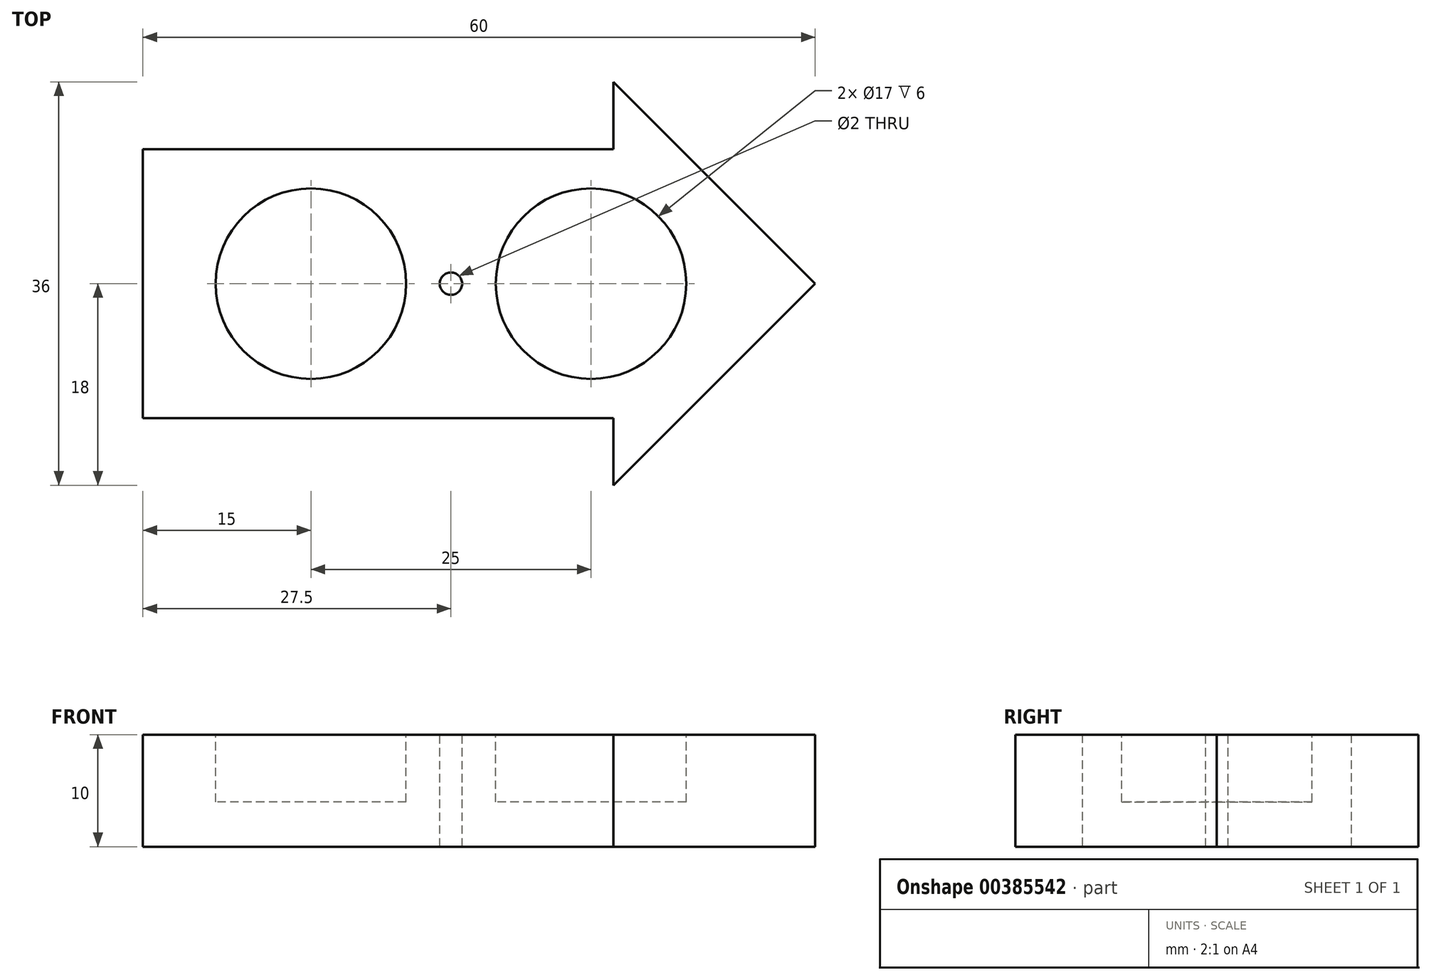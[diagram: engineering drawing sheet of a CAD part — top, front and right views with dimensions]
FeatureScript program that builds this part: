
annotation { "Feature Type Name" : "Feature", "Feature Type Description" : "" }
export const myFeature = defineFeature(function(context is Context, id is Id, definition is map)
    precondition{}
    {
        {
            var Q0;
            Q0=qCreatedBy(makeId("Top.planeOp"),FACE);
            var sketch = newSketch(context, id + "F0", { "sketchPlane" : qUnion([Q0])});
            skLineSegment(sketch, "E0.bottom", {"start": v(0, 0) * mm, "end": v(42, 0) * mm});
            skLineSegment(sketch, "E0.top", {"start": v(0, 24) * mm, "end": v(42, 24) * mm});
            skLineSegment(sketch, "E0.left", {"start": v(0, 0) * mm, "end": v(0, 24) * mm});
            skLineSegment(sketch, "E0.right", {"start": v(42, 0) * mm, "end": v(42, 24) * mm});
            skLineSegment(sketch, "E1.bottom", {"start": v(42, 30) * mm, "end": v(60, 30) * mm, "construction": true});
            skLineSegment(sketch, "E1.top", {"start": v(42, -6) * mm, "end": v(60, -6) * mm, "construction": true});
            skLineSegment(sketch, "E1.left", {"start": v(42, 30) * mm, "end": v(42, -6) * mm});
            skLineSegment(sketch, "E1.right", {"start": v(60, 30) * mm, "end": v(60, -6) * mm, "construction": true});
            skLineSegment(sketch, "E2", {"start": v(60, 12) * mm, "end": v(42, 30) * mm});
            skLineSegment(sketch, "E3", {"start": v(60, 12) * mm, "end": v(42, -6) * mm});
            skSolve(sketch);
        }
        {
            var Q0;
            Q0 = qSketchRegion(id + "F0", true);
            extrude(context, id + "F1", {"entities" : qUnion([Q0]), "depth" : 10 * mm});
        }
        {
            var Q0;
            Q0=makeQuery(id+"F1.opExtrude","CAP_FACE",FACE,{"disambiguationData":[OSD([sQuery(id+"F0.wireOp",EDGE,"E0.bottom"),sQuery(id+"F0.wireOp",EDGE,"E0.top"),sQuery(id+"F0.wireOp",EDGE,"E0.left"),sQuery(id+"F0.wireOp",EDGE,"E1.left"),sQuery(id+"F0.wireOp",EDGE,"E2"),sQuery(id+"F0.wireOp",EDGE,"E3")])],"isStart":false});
            var sketch = newSketch(context, id + "F2", { "sketchPlane" : qUnion([Q0])});
            skCircle(sketch, "E4", {"center": v(15, 12) * mm, "radius": 8.5 * mm});
            skPoint(sketch, "E4.centerSnap0", {"position": v(0, 12) * mm});
            skCircle(sketch, "E5", {"center": v(40, 12) * mm, "radius": 8.5 * mm});
            skSolve(sketch);
        }
        {
            var Q0;
            Q0 = qSketchRegion(id + "F2", true);
            extrude(context, id + "F3", {"entities" : qUnion([Q0]), "operationType" : NewBodyOperationType.REMOVE, "oppositeDirection" : true, "depth" : 6 * mm});
        }
        {
            var Q0;
            Q0=makeQuery(id+"F1.opExtrude","CAP_FACE",FACE,{"disambiguationData":[OSD([sQuery(id+"F0.wireOp",EDGE,"E0.bottom"),sQuery(id+"F0.wireOp",EDGE,"E0.top"),sQuery(id+"F0.wireOp",EDGE,"E0.left"),sQuery(id+"F0.wireOp",EDGE,"E1.left"),sQuery(id+"F0.wireOp",EDGE,"E2"),sQuery(id+"F0.wireOp",EDGE,"E3")])],"isStart":false});
            var sketch = newSketch(context, id + "F4", { "sketchPlane" : qUnion([Q0])});
            skLineSegment(sketch, "E6", {"start": v(15, 12) * mm, "end": v(28.13, 12) * mm, "construction": true});
            skCircle(sketch, "E7", {"center": v(27.5, 12) * mm, "radius": 1 * mm});
            skSolve(sketch);
        }
        {
            var Q0;
            Q0 = qSketchRegion(id + "F4", true);
            extrude(context, id + "F5", {"entities" : qUnion([Q0]), "operationType" : NewBodyOperationType.REMOVE, "oppositeDirection" : true, "depth" : 25 * mm});
        }
    });
